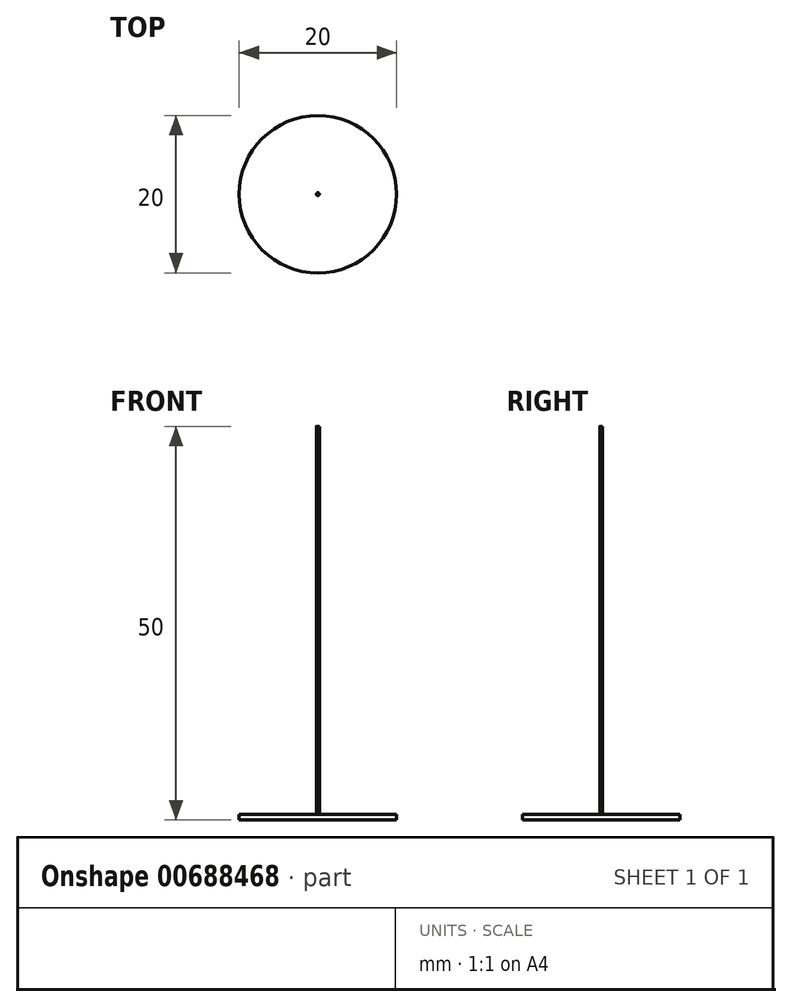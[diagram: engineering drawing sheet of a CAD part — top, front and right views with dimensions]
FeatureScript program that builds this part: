
annotation { "Feature Type Name" : "Feature", "Feature Type Description" : "" }
export const myFeature = defineFeature(function(context is Context, id is Id, definition is map)
    precondition{}
    {
        {
            var Q0;
            Q0=qCreatedBy(makeId("Top.planeOp"),FACE);
            var sketch = newSketch(context, id + "F0", { "sketchPlane" : qUnion([Q0])});
            skCircle(sketch, "E0", {"center": v(0, 0) * mm, "radius": 10 * mm});
            skSolve(sketch);
        }
        {
            var Q0;
            Q0 = qSketchRegion(id + "F0", true);
            extrude(context, id + "F1", {"entities" : qUnion([Q0]), "depth" : .7 * mm, "offsetDistance" : 25 * mm});
        }
        {
            var Q0;
            Q0=qCreatedBy(makeId("Top.planeOp"),FACE);
            var sketch = newSketch(context, id + "F2", { "sketchPlane" : qUnion([Q0])});
            skCircle(sketch, "E1", {"center": v(0, 0) * mm, "radius": 0.18 * mm});
            skSolve(sketch);
        }
        {
            var Q0;
            Q0 = qSketchRegion(id + "F2", true);
            extrude(context, id + "F3", {"entities" : qUnion([Q0]), "operationType" : NewBodyOperationType.ADD, "depth" : 50 * mm, "offsetDistance" : 25 * mm});
        }
    });
